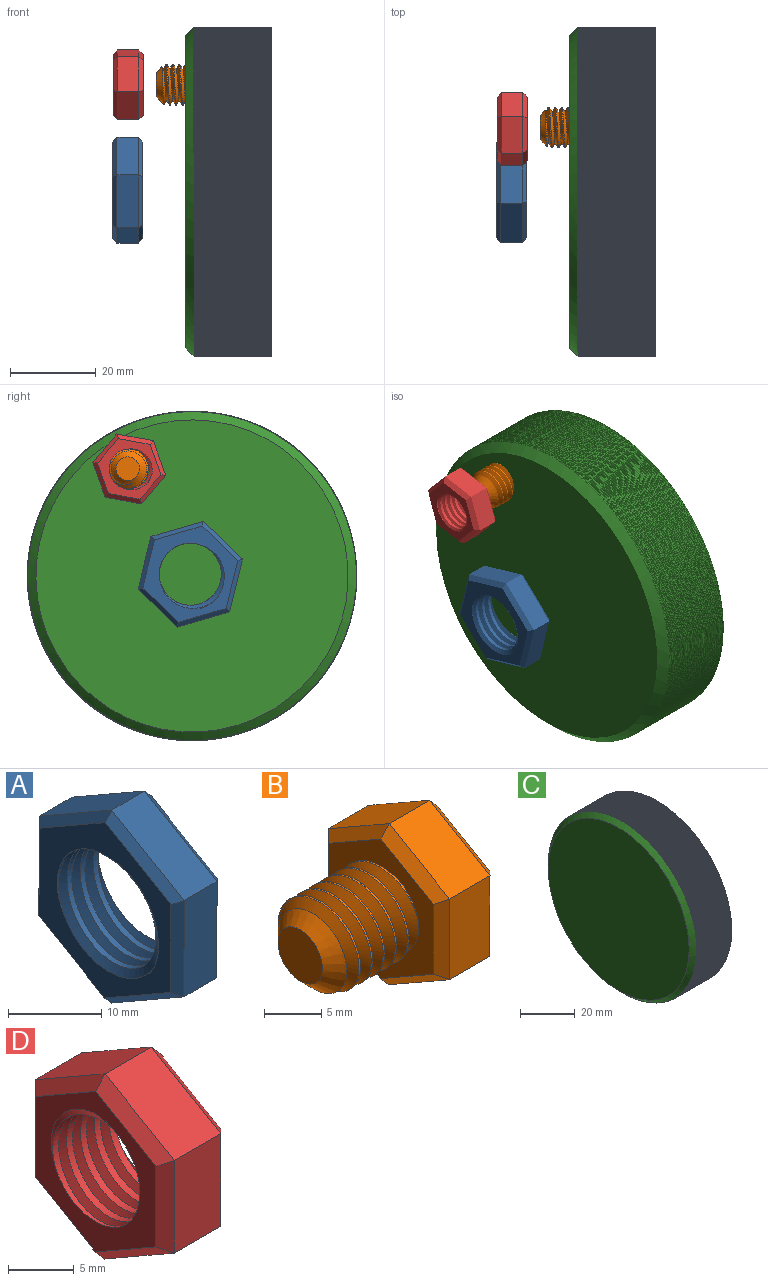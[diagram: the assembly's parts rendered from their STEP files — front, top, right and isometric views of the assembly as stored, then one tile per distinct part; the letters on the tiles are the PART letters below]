
ASSEMBLY  parts=4 mates=2
PART A: 23 faces, bbox 9.3x22.7x26 mm
  f0: cylinder r=7.24mm len=14.48mm, axis (1,0,0), area 111.6mm2, adj f7,f8,f21,f22
  f1: plane 10.98x6.38mm, normal (0,-0.5,0.86), area 63.5mm2, adj f2,f6,f14,f18
  f2: plane 12.7x5mm, normal (0,-1,0), area 63.5mm2, adj f1,f3,f12,f16
  f3: plane 11.02x6.32mm, normal (0,-0.5,-0.87), area 63.5mm2, adj f2,f4,f10,f15
  f4: plane 10.98x6.38mm, normal (0,0.5,-0.86), area 63.5mm2, adj f3,f5,f9,f17
  f5: plane 12.7x5mm, normal (0,1,0), area 63.5mm2, adj f4,f6,f11,f19
  f6: plane 11.02x6.32mm, normal (0,0.5,0.87), area 63.5mm2, adj f1,f5,f13,f20
  f7: plane 23.73x20.67mm, normal (-1,0,0), area 164.4mm2, adj f0,f9,f10,f11,f12,f13,f14,f21
  f8: plane 23.73x20.67mm, normal (1,0,0), area 164.4mm2, adj f0,f15,f16,f17,f18,f19,f20,f21
  f9: plane 10.99x6.96mm, normal (-0.71,0.36,-0.61), area 17.1mm2, adj f4,f7,f10,f11
  f10: plane 11.02x6.9mm, normal (-0.71,-0.35,-0.61), area 17.1mm2, adj f3,f7,f9,f12
  f11: plane 12.7x1.03mm, normal (-0.71,0.71,0), area 17.1mm2, adj f5,f7,f9,f13
  f12: plane 12.7x1.03mm, normal (-0.71,-0.71,0), area 17.1mm2, adj f2,f7,f10,f14
  f13: plane 11.02x6.9mm, normal (-0.71,0.35,0.61), area 17.1mm2, adj f6,f7,f11,f14
  f14: plane 10.99x6.96mm, normal (-0.71,-0.36,0.61), area 17.1mm2, adj f1,f7,f12,f13
  f15: plane 11.02x6.9mm, normal (0.71,-0.35,-0.61), area 17.1mm2, adj f3,f8,f16,f17
  f16: plane 12.7x1.03mm, normal (0.71,-0.71,0), area 17.1mm2, adj f2,f8,f15,f18
  f17: plane 10.99x6.96mm, normal (0.71,0.36,-0.61), area 17.1mm2, adj f4,f8,f15,f19
  f18: plane 10.99x6.96mm, normal (0.71,-0.36,0.61), area 17.1mm2, adj f1,f8,f16,f20
  f19: plane 12.7x1.03mm, normal (0.71,0.71,0), area 17.1mm2, adj f5,f8,f17,f20
  f20: plane 11.02x6.9mm, normal (0.71,0.35,0.61), area 17.1mm2, adj f6,f8,f18,f19
  f21: bspline ~19.31x16.73mm, area 223mm2, adj f0,f7,f8,f22
  f22: bspline ~19.31x16.73mm, area 223mm2, adj f0,f7,f8,f21
PART B: 25 faces, bbox 17.8x15.9x18.1 mm
  f0: cylinder r=4.75mm len=9.5mm, axis (1,0,0), area 28.1mm2, adj f1,f2,f4,f12
  f1: bspline ~10.97x9.91mm, area 196.7mm2, adj f0,f2,f4,f12
  f2: bspline ~10.97x10.66mm, area 196.6mm2, adj f0,f1,f4,f12
  f3: plane 5.5x5.5mm, normal (-1,0,0), area 23.8mm2, adj f4
  f4: cone r=4.75mm half-angle=45deg, axis (1,0,0), area 47.4mm2, adj f0,f1,f2,f3
  f5: plane 7.48x5mm, normal (0,-0.5,0.86), area 43.3mm2, adj f6,f10,f18,f22
  f6: plane 8.66x5mm, normal (0,-1,0), area 43.3mm2, adj f5,f7,f16,f20
  f7: plane 7.52x5mm, normal (0,-0.5,-0.87), area 43.3mm2, adj f6,f8,f14,f19
  f8: plane 7.48x5mm, normal (0,0.5,-0.86), area 43.3mm2, adj f7,f9,f13,f21
  f9: plane 8.66x5mm, normal (0,1,0), area 43.3mm2, adj f8,f10,f15,f23
  f10: plane 7.52x5mm, normal (0,0.5,0.87), area 43.3mm2, adj f5,f9,f17,f24
  f11: plane 15.01x13.03mm, normal (1,0,0), area 146.4mm2, adj f13,f14,f15,f16,f17,f18
  f12: plane 15.83x13.85mm, normal (-1,0,0), area 89.2mm2, adj f0,f1,f2,f19,f20,f21,f22,f23
  f13: plane 7.49x4.93mm, normal (0.71,0.36,-0.61), area 11.4mm2, adj f8,f11,f14,f15
  f14: plane 7.52x4.88mm, normal (0.71,-0.35,-0.61), area 11.4mm2, adj f7,f11,f13,f16
  f15: plane 8.66x1.03mm, normal (0.71,0.71,0), area 11.4mm2, adj f9,f11,f13,f17
  f16: plane 8.66x1.03mm, normal (0.71,-0.71,0), area 11.4mm2, adj f6,f11,f14,f18
  f17: plane 7.52x4.88mm, normal (0.71,0.35,0.61), area 11.4mm2, adj f10,f11,f15,f18
  f18: plane 7.49x4.93mm, normal (0.71,-0.36,0.61), area 11.4mm2, adj f5,f11,f16,f17
  f19: plane 7.52x4.88mm, normal (-0.71,-0.35,-0.61), area 11.4mm2, adj f7,f12,f20,f21
  f20: plane 8.66x1.03mm, normal (-0.71,-0.71,0), area 11.4mm2, adj f6,f12,f19,f22
  f21: plane 7.49x4.93mm, normal (-0.71,0.36,-0.61), area 11.4mm2, adj f8,f12,f19,f23
  f22: plane 7.49x4.93mm, normal (-0.71,-0.36,0.61), area 11.4mm2, adj f5,f12,f20,f24
  f23: plane 8.66x1.03mm, normal (-0.71,0.71,0), area 11.4mm2, adj f9,f12,f21,f24
  f24: plane 7.52x4.88mm, normal (-0.71,0.35,0.61), area 11.4mm2, adj f10,f12,f22,f23
PART C: 8 faces, bbox 20.6x89.3x77.4 mm
  f0: cylinder r=38.4mm len=76.8mm, axis (1,0,0), area -5862mm2, adj f2,f3,f4,f5,f6,f7
  f1: plane 72.8x72.8mm, normal (-1,0,0), area 4162.5mm2, adj f3
  f2: plane 77.38x77.36mm, normal (1,0,0), area 4627.9mm2, adj f0,f5,f7
  f3: cone r=38.4mm half-angle=45deg, axis (1,0,0), area 653.2mm2, adj f0,f1,f4,f6,f7
  f4: cone r=38.4mm half-angle=45deg, axis (1,0,0), area 0.2mm2, adj f0,f3,f7
  f5: plane 0.08x0.04mm, normal (0,1,0), area 0mm2, adj f0,f2,f6
  f6: bspline ~88.68x76.8mm, area 3809.6mm2, adj f0,f3,f5,f7
  f7: bspline ~88.68x76.8mm, area 3808.8mm2, adj f0,f2,f3,f4,f6
PART D: 23 faces, bbox 9.1x15.4x17.7 mm
  f0: plane 7.49x5mm, normal (0,-0.5,0.86), area 43.3mm2, adj f1,f5,f13,f17
  f1: plane 8.66x5mm, normal (0,-1,0), area 43.3mm2, adj f0,f2,f11,f15
  f2: plane 7.51x5mm, normal (0,-0.5,-0.87), area 43.3mm2, adj f1,f3,f9,f14
  f3: plane 7.49x5mm, normal (0,0.5,-0.86), area 43.3mm2, adj f2,f4,f8,f16
  f4: plane 8.66x5mm, normal (0,1,0), area 43.3mm2, adj f3,f5,f10,f18
  f5: plane 7.51x5mm, normal (0,0.5,0.87), area 43.3mm2, adj f0,f4,f12,f19
  f6: plane 15.37x13.38mm, normal (-1,0,0), area 71.4mm2, adj f8,f9,f10,f11,f12,f13,f20,f21
  f7: plane 15.37x13.38mm, normal (1,0,0), area 71.4mm2, adj f14,f15,f16,f17,f18,f19,f20,f21
  f8: plane 7.49x4.93mm, normal (-0.71,0.36,-0.61), area 11.4mm2, adj f3,f6,f9,f10
  f9: plane 7.51x4.89mm, normal (-0.71,-0.35,-0.61), area 11.4mm2, adj f2,f6,f8,f11
  f10: plane 8.66x1.02mm, normal (-0.71,0.71,0), area 11.4mm2, adj f4,f6,f8,f12
  f11: plane 8.66x1.02mm, normal (-0.71,-0.71,0), area 11.4mm2, adj f1,f6,f9,f13
  f12: plane 7.51x4.89mm, normal (-0.71,0.35,0.61), area 11.4mm2, adj f5,f6,f10,f13
  f13: plane 7.49x4.93mm, normal (-0.71,-0.36,0.61), area 11.4mm2, adj f0,f6,f11,f12
  f14: plane 7.51x4.89mm, normal (0.71,-0.35,-0.61), area 11.4mm2, adj f2,f7,f15,f16
  f15: plane 8.66x1.02mm, normal (0.71,-0.71,0), area 11.4mm2, adj f1,f7,f14,f17
  f16: plane 7.49x4.93mm, normal (0.71,0.36,-0.61), area 11.4mm2, adj f3,f7,f14,f18
  f17: plane 7.49x4.93mm, normal (0.71,-0.36,0.61), area 11.4mm2, adj f0,f7,f15,f19
  f18: plane 8.66x1.02mm, normal (0.71,0.71,0), area 11.4mm2, adj f4,f7,f16,f19
  f19: plane 7.51x4.89mm, normal (0.71,0.35,0.61), area 11.4mm2, adj f5,f7,f17,f18
  f20: cylinder r=4.66mm len=9.32mm, axis (1,0,0), area 85.4mm2, adj f6,f7,f21,f22
  f21: bspline ~12.5x10.82mm, area 128.4mm2, adj f6,f7,f20,f22
  f22: bspline ~12.5x10.82mm, area 128.5mm2, adj f6,f7,f20,f21
PLACE A rot(axis=(0,0.6,-0.8),180deg) t=(-55.27,-6.86,23.48)mm fixed
PLACE B rot(axis=(-1,0,0),43.8deg) t=(-31.66,7.73,48.08)mm
PLACE C rot(axis=(1,0,0),109.9deg) t=(-18.27,-7.25,23.06)mm
PLACE D rot(axis=(1,0,0),100.2deg) t=(-48.16,7.38,48.02)mm fixed
MATE cylindrical C.f0 <-> A.f7  axis (-1,0,0) through (-38.27,-7.25,23.06)mm
MATE cylindrical B.f0 <-> D.f6  axis (-1,0,0) through (-45.16,7.73,48.08)mm
